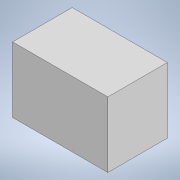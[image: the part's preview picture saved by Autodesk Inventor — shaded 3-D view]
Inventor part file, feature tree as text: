
AUTODESK INVENTOR PART (.ipt)
format: ipt  version: 2020 (Build 240168000, 168)  size: 84,480 bytes
history: native  units: mm
features: extrude x1, sketch x1
ambient origin geometry x8: Origin, YZ Plane, XZ Plane, XY Plane, X Axis, Y Axis, Z Axis, Center Point
bodies: Solid1 (feature_tree)
feature tree (2):
  extrude  "Extrusion1"  Depth=160.0mm
  sketch  "Sketch1"  dims[d0=110.0mm d1=160.0mm d2=100.0mm d3=0.0mm]
